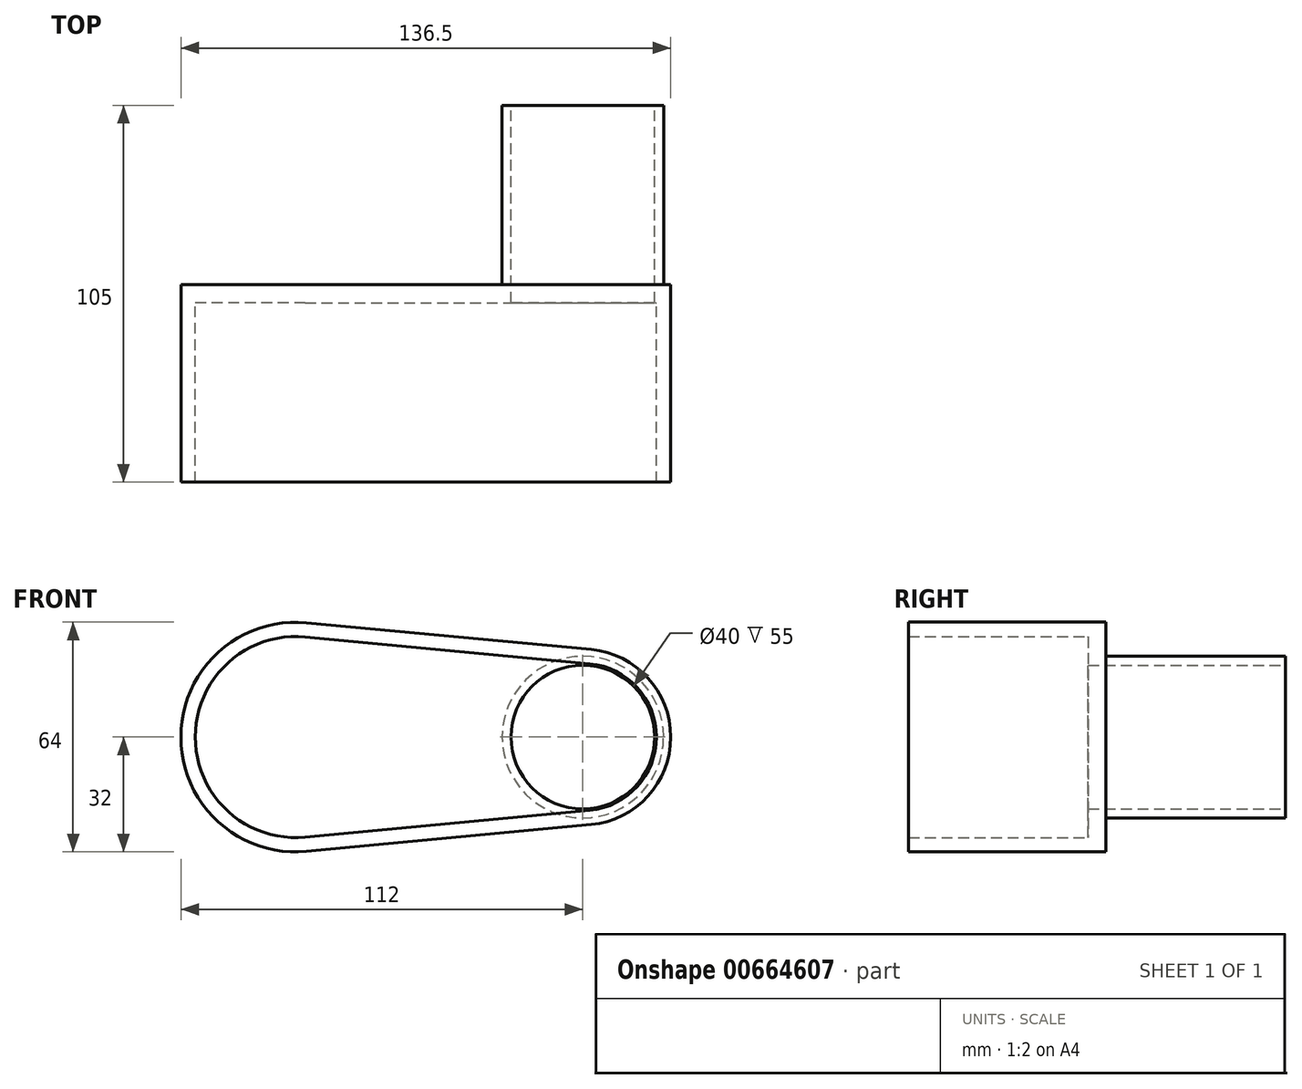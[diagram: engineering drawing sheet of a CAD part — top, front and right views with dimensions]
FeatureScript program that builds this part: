
annotation { "Feature Type Name" : "Feature", "Feature Type Description" : "" }
export const myFeature = defineFeature(function(context is Context, id is Id, definition is map)
    precondition{}
    {
        {
            var Q0;
            Q0=qCreatedBy(makeId("Front.planeOp"),FACE);
            var sketch = newSketch(context, id + "F0", { "sketchPlane" : qUnion([Q0])});
            skLineSegment(sketch, "E0", {"start": v(-40, 0) * mm, "end": v(40, 0) * mm, "construction": true});
            skCircle(sketch, "E1", {"center": v(40, 0) * mm, "radius": 22.5 * mm});
            skCircle(sketch, "E2", {"center": v(-40, 0) * mm, "radius": 30 * mm});
            skLineSegment(sketch, "E3", {"start": v(-37.19, 29.87) * mm, "end": v(42.1, 22.4) * mm});
            skLineSegment(sketch, "E4", {"start": v(-37.19, -29.87) * mm, "end": v(42.1, -22.4) * mm});
            skCircle(sketch, "E5", {"center": v(40, 0) * mm, "radius": 20 * mm});
            skSolve(sketch);
        }
        {
            var Q0;
            {var subQ0=sQuery(id+"F0.wireOp",EDGE,"E2");var subQ1=makeQuery(id+"F0.imprint","INTERSECT",VERTEX,{"derivedFrom":[subQ0,sQuery(id+"F0.wireOp",EDGE,"E3")]});Q0=makeQuery(id+"F0.imprint","IMPRINT",FACE,{"disambiguationData":[TD([[makeQuery(id+"F0.imprint","IMPRINT",EDGE,{"disambiguationData":[TD([[subQ1,-1.0]])],"derivedFrom":subQ0}),1.0]])]});}
            var Q1;
            {var subQ0=sQuery(id+"F0.wireOp",EDGE,"E3");Q1=makeQuery(id+"F0.imprint","IMPRINT",FACE,{"disambiguationData":[TD([[makeQuery(id+"F0.imprint","IMPRINT",EDGE,{"derivedFrom":subQ0}),-1.0]])]});}
            var Q2;
            Q2=makeQuery(id+"F0.imprint","IMPRINT",FACE,{"disambiguationData":[TD([[makeQuery(id+"F0.imprint","IMPRINT",EDGE,{"derivedFrom":sQuery(id+"F0.wireOp",EDGE,"E5")}),-1.0]])]});
            extrude(context, id + "F1", {"entities" : qUnion([Q0, Q1, Q2]), "depth" : 5 * mm, "offsetDistance" : 25 * mm});
        }
        {
            var Q0;
            Q0=makeQuery(id+"F0.imprint","IMPRINT",FACE,{"disambiguationData":[TD([[makeQuery(id+"F0.imprint","IMPRINT",EDGE,{"derivedFrom":sQuery(id+"F0.wireOp",EDGE,"E5")}),-1.0]])]});
            extrude(context, id + "F2", {"entities" : qUnion([Q0]), "operationType" : NewBodyOperationType.ADD, "oppositeDirection" : true, "depth" : 50 * mm, "offsetDistance" : 25 * mm});
        }
        {
            var Q0;
            Q0=makeQuery(id+"F1.opExtrude","CAP_FACE",FACE,{"disambiguationData":[OSD([sQuery(id+"F0.wireOp",EDGE,"E1"),sQuery(id+"F0.wireOp",EDGE,"E2"),sQuery(id+"F0.wireOp",EDGE,"E3"),sQuery(id+"F0.wireOp",EDGE,"E4"),sQuery(id+"F0.wireOp",EDGE,"E5")])],"isStart":false});
            var sketch = newSketch(context, id + "F3", { "sketchPlane" : qUnion([Q0])});
            skLineSegment(sketch, "E6.0", {"start": v(-37, -31.86) * mm, "end": v(42.3, -24.4) * mm});
            skArc(sketch, "E6.1", {"start": v(-37, 31.86) * mm, "mid": v(-72, 0) * mm, "end": v(-37, -31.86) * mm});
            skLineSegment(sketch, "E6.2", {"start": v(-37, 31.86) * mm, "end": v(42.3, 24.4) * mm});
            skArc(sketch, "E6.3", {"start": v(42.3, -24.4) * mm, "mid": v(64.5, 0) * mm, "end": v(42.3, 24.4) * mm});
            skArc(sketch, "E7.0", {"start": v(-37.38, 27.88) * mm, "mid": v(-68, 0) * mm, "end": v(-37.38, -27.88) * mm});
            skLineSegment(sketch, "E7.1", {"start": v(-37.38, 27.88) * mm, "end": v(41.92, 20.4) * mm});
            skArc(sketch, "E7.2", {"start": v(41.92, -20.4) * mm, "mid": v(60.5, 0) * mm, "end": v(41.92, 20.4) * mm});
            skLineSegment(sketch, "E7.3", {"start": v(-37.38, -27.88) * mm, "end": v(41.92, -20.4) * mm});
            skSolve(sketch);
        }
        {
            var Q0;
            Q0=makeQuery(id+"F3.imprint","IMPRINT",FACE,{"disambiguationData":[TD([[makeQuery(id+"F3.imprint","IMPRINT",EDGE,{"derivedFrom":sQuery(id+"F3.wireOp",EDGE,"E6.0")}),1.0]])]});
            extrude(context, id + "F4", {"entities" : qUnion([Q0]), "oppositeDirection" : true, "depth" : 5 * mm, "offsetDistance" : 25 * mm});
        }
        {
            var Q0;
            Q0=makeQuery(id+"F3.imprint","IMPRINT",FACE,{"disambiguationData":[TD([[makeQuery(id+"F3.imprint","IMPRINT",EDGE,{"derivedFrom":sQuery(id+"F3.wireOp",EDGE,"E7.0")}),-1.0]])]});
            var Q1;
            Q1=makeQuery(id+"F3.imprint","IMPRINT",FACE,{"disambiguationData":[TD([[makeQuery(id+"F3.imprint","IMPRINT",EDGE,{"derivedFrom":sQuery(id+"F3.wireOp",EDGE,"E6.0")}),1.0]])]});
            extrude(context, id + "F5", {"entities" : qUnion([Q0, Q1]), "operationType" : NewBodyOperationType.ADD, "depth" : 50 * mm, "offsetDistance" : 25 * mm});
        }
    });
